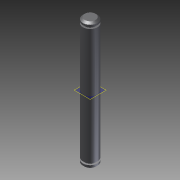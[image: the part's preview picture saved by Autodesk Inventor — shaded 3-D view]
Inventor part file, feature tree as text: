
AUTODESK INVENTOR PART (.ipt)
format: ipt  version: 2011 (Build 150229000, 229)  size: 95,744 bytes
history: native  units: mm (DEFAULTED — no unit token found)
features: revolve x1, plane x1, sketch x1
ambient origin geometry x8: Origin, YZ Plane, XZ Plane, XY Plane, X Axis, Y Axis, Z Axis, Center Point
feature tree (3):
  revolve  "Revolution1"  [1 undecoded]
  plane  "Work Plane1"
  sketch  "Sketch1"  dims[d4=65.0mm d5=1.0mm d6=66.0mm d7=2.0mm d18=90.0deg d19=8.0mm d20=45.0deg d23=1.0mm d24=1.0mm]
note: 1 required parameter value undecoded (feature->parameter linkage not recoverable at this tier; creation-order binding heuristic only, values carry confidence <= 0.55)
